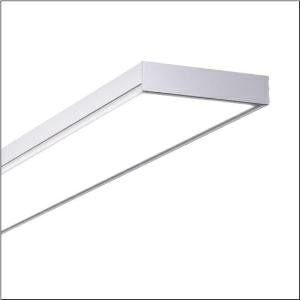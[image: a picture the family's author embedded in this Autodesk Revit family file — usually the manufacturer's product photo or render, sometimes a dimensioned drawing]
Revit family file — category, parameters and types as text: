
# Revit family: apollon_r__31_surface_51mp25wm2441ea_65a1
name_source: partatom
category: Lighting Fixtures
units: mm (PartAtom-declared; Revit-internal decimal feet)

## family parameters
Cut with Voids When Loaded = No
Host = Face
Light Source = No
Part Type = Normal
Room Calculation Point = No
Round Connector Dimension = Use Diameter
Shared = No

## types (1)
- Apollon® 31 Surface (1 x LED, 3800 lm, 27 W, 4000K)
    Apparent Load = 27 VA
    CIE Flux Codes = 61 87 97 97 100
    Color Rendering = 80
    Color Temperature = 4000K
    Default Elevation = 1800 mm
    Description = Apollon® 31 Surface, office luminaire, primary optical cover: micro prismatic cover, of PMMA, light emission: direct distribution, primary light characteristic: symmetric, installation type: surface-mounted, LED, rated luminous flux: 3.800lm, luminous efficacy: 139lm/W, light colour: 840, colour temperature: 4000K, control gear: ECG Multilumen, with terminal, 3-pole, mains connection: 220..240V, AC, 50/60Hz, rated input power: 27W, housing, of sheet steel, coil coated, metallic grey (RAL 9006), length: 1.245mm, width: 200mm, height: 44mm, protection rating (complete): IP20, insulation class (complete): insulation class II (safety insulation), certification: CE, impact resistance: IK02, permissible operating ambient temperature: -20..+40°C, packaging unit: 1 piece
    Height = 44 mm
    Lamp = 1 x LED
    Lamp Light Flux = 3800 lm
    Lamp Power = 27 W
    Lamp count = 1
    Length = 1245 mm
    Luminous efficacy = 141 lm/W
    Manufacturer = Siteco
    ModVariant = No
    Model = 51MP25WM2441EA
    Mounting Place = Ceiling
    Mounting Type = Surface mounted
    Number of Poles = 1
    OnlyDefault = Yes
    Power Factor = 1
    Product Name = Apollon® 31 Surface
    Product group = office luminaire | ceiling mounted
    ProductGroupID = 300
    Protection Class = Protection class II
    Protection Degree = IP 20
    RLX_Detail_Level = 1
    RLX_Emergency_Light_Flux = 0 lm
    RLX_Emergency_Type = 0
    RLX_Emergency_Type_DB = No
    RlxData = <blob elided: 24081 chars, md5=53f1e2ce>
    Socket = socket
    Standby Power = 0 W
    System Light Flux = 3800 lm
    System Power = 27 W
    Type Comments = Product without accessories
    Type Image = l_1313654.jpg
    URL = http://relux.com
    VarID = ---
    Voltage = 0 V
    Weight = 0.00 kg
    Width = 200 mm  [stored 0.656168 ft]

note: [stored X ft] marks values corroborated as IEEE doubles in the binary element streams (Revit-internal decimal feet)

## geometry (parser evidence)
native form markers: Blend x4, Sweep x11
no freeform markers — native parametric forms only
